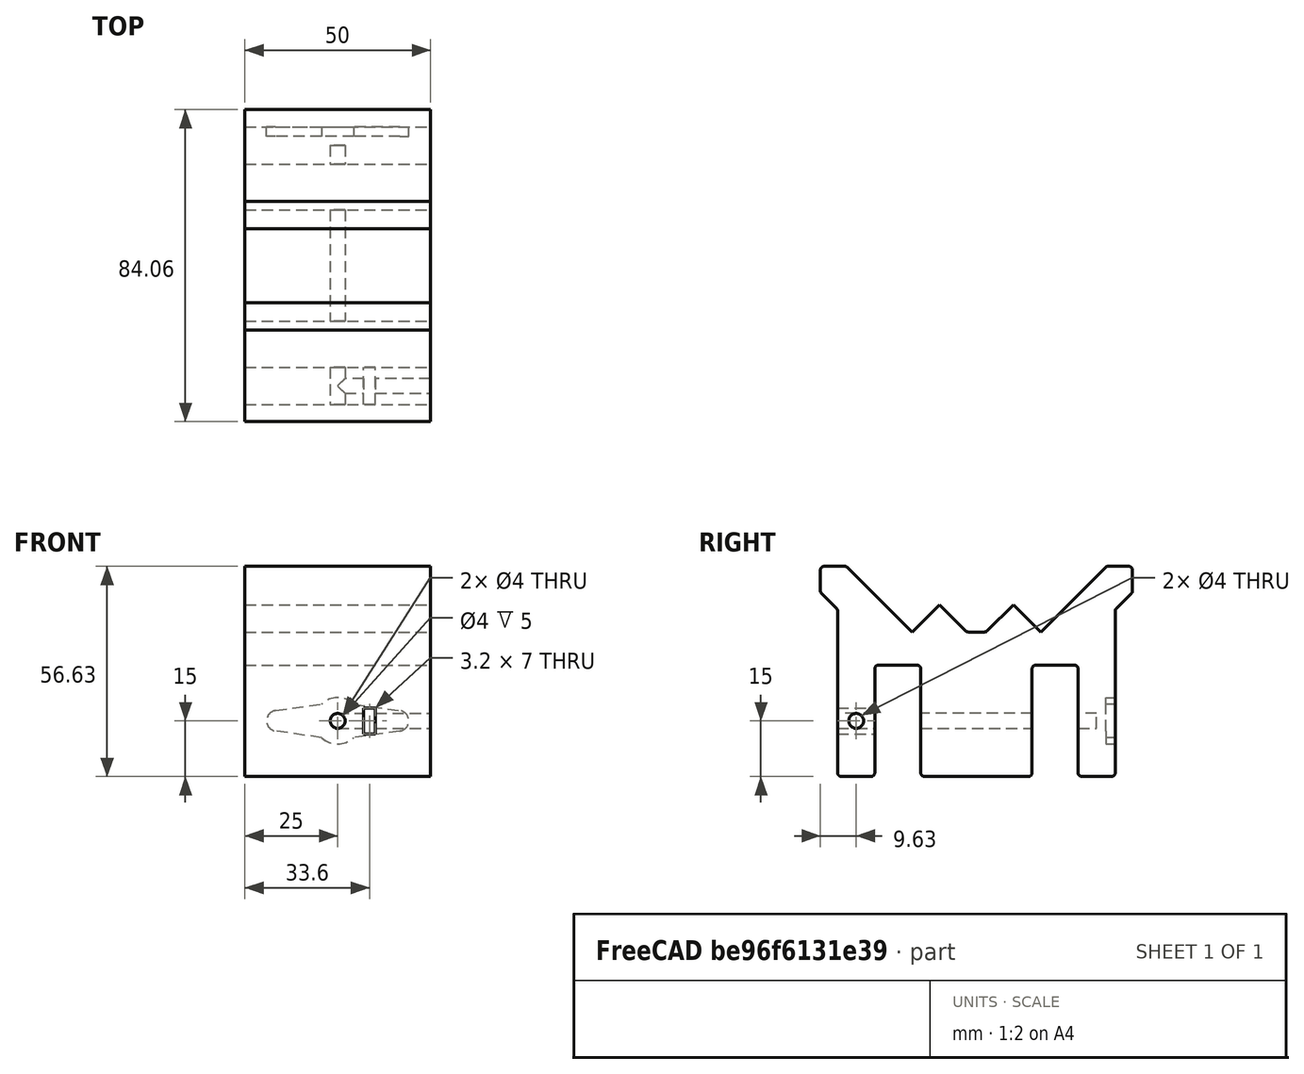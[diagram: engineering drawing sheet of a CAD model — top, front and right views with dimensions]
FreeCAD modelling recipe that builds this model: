
FCSTD DOCUMENT  (FreeCAD 0.19R24267 +99 (Git))
Label: Lager
License: All rights reserved
LicenseURL: http://en.wikipedia.org/wiki/All_rights_reserved
objects: TechDraw::DrawViewDimension×24, Sketcher::SketchObject×5, PartDesign::Pocket×4, PartDesign::Fillet×3, TechDraw::DrawProjGroupItem×3, PartDesign::Pad×1, PartDesign::Body×1, TechDraw::DrawSVGTemplate×1, TechDraw::DrawProjGroup×1, TechDraw::DrawPage×1
note: 22 computed .brp shape members not serialized (recipe doc carries the construction recipe); baked Part::Feature solids carry a one-line shape summary decoded from their .brp

FEATURE [Sketcher::SketchObject] Sketch
  FullyConstrained = true
  MapMode = 5
  Placement = pos=(0,0,0) rot=(0.57735,0.57735,0.57735;2.0944rad)
  Support = -> [YZ_Plane]
  sketch-geometry (29):
    g0: LineSegment StartX=-37.4 StartY=0 StartZ=0 EndX=-37.4 EndY=45 EndZ=0
    g1: LineSegment StartX=-37.4 StartY=45 StartZ=0 EndX=-42.0316 EndY=49.6316 EndZ=0
    g2: LineSegment StartX=-42.0316 StartY=49.6316 StartZ=0 EndX=-42.0316 EndY=56.6316 EndZ=0
    g3: LineSegment StartX=-42.0316 StartY=56.6316 StartZ=0 EndX=-35.0316 EndY=56.6316 EndZ=0
    g4: LineSegment StartX=-35.0316 StartY=56.6316 StartZ=0 EndX=-17.3539 EndY=38.9539 EndZ=0
    g5: LineSegment StartX=-17.3539 StartY=38.9539 StartZ=0 EndX=-10 EndY=46.3078 EndZ=0
    g6: LineSegment StartX=-10 StartY=46.3078 StartZ=0 EndX=-2.64609 EndY=38.9539 EndZ=0
    g7: LineSegment StartX=-2.64609 StartY=38.9539 StartZ=0 EndX=2.64609 EndY=38.9539 EndZ=0
    g8: LineSegment StartX=2.64609 StartY=38.9539 StartZ=0 EndX=10 EndY=46.3078 EndZ=0
    g9: LineSegment StartX=10 StartY=46.3078 StartZ=0 EndX=17.3539 EndY=38.9539 EndZ=0
    g10: LineSegment StartX=17.3539 StartY=38.9539 StartZ=0 EndX=35.0316 EndY=56.6316 EndZ=0
    g11: LineSegment StartX=35.0316 StartY=56.6316 StartZ=0 EndX=42.0316 EndY=56.6316 EndZ=0
    g12: LineSegment StartX=42.0316 StartY=56.6316 StartZ=0 EndX=42.0316 EndY=49.6316 EndZ=0
    g13: LineSegment StartX=42.0316 StartY=49.6316 StartZ=0 EndX=37.4 EndY=45 EndZ=0
    g14: LineSegment StartX=37.4 StartY=45 StartZ=0 EndX=37.4 EndY=0 EndZ=0
    g15: LineSegment StartX=37.4 StartY=0 StartZ=0 EndX=27.4 EndY=0 EndZ=0
    g16: LineSegment StartX=27.4 StartY=0 StartZ=0 EndX=27.4 EndY=30 EndZ=0
    g17: LineSegment StartX=27.4 StartY=30 StartZ=0 EndX=15 EndY=30 EndZ=0
    g18: LineSegment StartX=15 StartY=30 StartZ=0 EndX=15 EndY=0 EndZ=0
    g19: LineSegment StartX=15 StartY=0 StartZ=0 EndX=-15 EndY=0 EndZ=0
    g20: LineSegment StartX=-15 StartY=0 StartZ=0 EndX=-15 EndY=30 EndZ=0
    g21: LineSegment StartX=-15 StartY=30 StartZ=0 EndX=-27.4 EndY=30 EndZ=0
    g22: LineSegment StartX=-27.4 StartY=30 StartZ=0 EndX=-27.4 EndY=0 EndZ=0
    g23: LineSegment StartX=-27.4 StartY=0 StartZ=0 EndX=-37.4 EndY=0 EndZ=0
    g24: Circle CenterX=0 CenterY=61.0566 CenterZ=0 NormalX=0 NormalY=0 NormalZ=1 AngleXU=0 Radius=17.5
    g25: LineSegment StartX=10 StartY=46.3078 StartZ=0 EndX=27.6777 EndY=63.9855 EndZ=0
    g26: LineSegment StartX=-10 StartY=46.3078 StartZ=0 EndX=-27.6777 EndY=63.9855 EndZ=0
    g27: LineSegment StartX=35.0316 StartY=56.6316 StartZ=0 EndX=27.6777 EndY=63.9855 EndZ=0
    g28: LineSegment StartX=-35.0316 StartY=56.6316 StartZ=0 EndX=-27.6777 EndY=63.9855 EndZ=0
  constraints (76):
    c: Vertical(g0)
    c: Coincident(g0,g1)
    c: Coincident(g1,g2)
    c: Coincident(g2,g3)
    c: Horizontal(g3)
    c: Coincident(g3,g4)
    c: Coincident(g4,g5)
    c: Coincident(g5,g6)
    c: Coincident(g6,g7)
    c: Coincident(g7,g8)
    c: Coincident(g8,g9)
    c: Coincident(g9,g10)
    c: Coincident(g10,g11)
    c: Coincident(g11,g12)
    c: Vertical(g12)
    c: Coincident(g12,g13)
    c: Coincident(g13,g14)
    c: Coincident(g14,g15)
    c: Coincident(g15,g16)
    c: Vertical(g16)
    c: Coincident(g16,g17)
    c: Horizontal(g17)
    c: Coincident(g17,g18)
    c: Vertical(g18)
    c: Coincident(g18,g19)
    c: Horizontal(g19)
    c: Coincident(g19,g20)
    c: Coincident(g20,g21)
    c: Coincident(g21,g22)
    c: Vertical(g22)
    c: Coincident(g22,g23)
    c: Coincident(g23,g0)
    c: Vertical(g20)
    c: Horizontal(g21)
    c: DistanceX(g17,g17) = 12.4
    c: Horizontal(g15)
    c: Horizontal(g23)
    c: Angle(g1,g0) = 2.35619
    c: Symmetric(g21,g16,g-2)
    c: Symmetric(g0,g14,g-2)
    c: DistanceX(g5,g8) = 20
    c: DistanceX(g19,g19) = 30
    c: DistanceX(g23,g23) = 10
    c: DistanceX(g10,g11) = 7
    c: DistanceY(g14,g14) = 45
    c: Symmetric(g13,g0,g-2)
    c: DistanceY(g12,g12) = 7
    c: Symmetric(g7,g6,g-2)
    c: Symmetric(g9,g4,g-2)
    c: DistanceY(g20,g20) = 30
    c: PointOnObject(g18,g-1)
    c: Parallel(g6,g1)
    c: Symmetric(g1,g12,g-2)
    c: Symmetric(g11,g2,g-2)
    c: Equal(g17,g21)
    c: Horizontal(g22,g19)
    c: Parallel(g1,g4)
    c: Angle(g5,g4) = 1.5708
    c: Distance(g4,g3) = 25
    c: Symmetric(g10,g3,g-2)
    c: Symmetric(g5,g8,g-2)
    c: Distance(g9) = 10.4
    c: Horizontal(g4,g6)
    c: PointOnObject(g24,g-2)
    c: Diameter(g24) = 35
    c: Coincident(g25,g8)
    c: Coincident(g26,g5)
    c: Coincident(g27,g10)
    c: Coincident(g27,g25)
    c: Coincident(g28,g3)
    c: Coincident(g28,g26)
    c: Equal(g10,g25)
    c: Equal(g9,g27)
    c: Equal(g4,g26)
    c: Equal(g28,g5)
    c: Tangent(g24,g25)
FEATURE [PartDesign::Pad] Pad
  Direction = (1,1,1)
  Length = 50
  Length2 = 100
  Placement = pos=(0,0,0) rot=(0.57735,0.57735,0.57735;2.0944rad)
  Profile = -> Sketch
  Type = 0
FEATURE [Sketcher::SketchObject] Sketch001
  ExternalGeometry = -> [Pad]
  FullyConstrained = true
  MapMode = 5
  Placement = pos=(-1.65e-14,-37.4,8.2e-15) rot=(-0.57735,-0.57735,0.57735;4.18879rad)
  Support = -> [Pad]
  sketch-geometry (2):
    g0: LineSegment StartX=-15 StartY=25 StartZ=0 EndX=-8.9e-15 EndY=25 EndZ=0
    g1: Circle CenterX=-15 CenterY=25 CenterZ=0 NormalX=0 NormalY=0 NormalZ=1 AngleXU=0 Radius=2
  constraints (5):
    c: Horizontal(g0)
    c: DistanceX(g0,g0) = 15
    c: Coincident(g1,g0)
    c: Symmetric(g-3,g-1,g0)
    c: Diameter(g1) = 4
FEATURE [PartDesign::Pocket] Pocket  label="Achsenloch"
  BaseFeature = -> Pad
  Length = 69.8
  Length2 = 100
  Offset = 2
  Placement = pos=(0,0,0) rot=(0.57735,0.57735,0.57735;2.0944rad)
  Profile = -> Sketch001
  Type = 0
  expr: Offset = 2
  expr: Length = 74.8 - 5
FEATURE [Sketcher::SketchObject] Sketch002
  ExternalGeometry = -> [Pocket]
  FullyConstrained = true
  MapMode = 5
  Placement = pos=(1.65e-14,37.4,-8.2e-15) rot=(0.57735,0.57735,0.57735;4.18879rad)
  Support = -> [Pocket]
  sketch-geometry (9):
    g0: LineSegment StartX=12.25 StartY=41.7602 StartZ=0 EndX=10.5 EndY=29.3373 EndZ=0
    g1: LineSegment StartX=10.5 StartY=20.6627 StartZ=0 EndX=12.25 EndY=8.23976 EndZ=0
    g2: ArcOfCircle CenterX=15 CenterY=8.62715 CenterZ=0 NormalX=0 NormalY=0 NormalZ=1 AngleXU=0 Radius=2.77715 StartAngle=3.28154 EndAngle=6.14324
    g3: LineSegment StartX=17.75 StartY=8.23976 StartZ=0 EndX=19.5 EndY=20.6627 EndZ=0
    g4: LineSegment StartX=19.5 StartY=29.3373 StartZ=0 EndX=17.75 EndY=41.7602 EndZ=0
    g5: ArcOfCircle CenterX=15 CenterY=41.3728 CenterZ=0 NormalX=0 NormalY=0 NormalZ=1 AngleXU=0 Radius=2.77715 StartAngle=0.139948 EndAngle=3.00164
    g6: ArcOfCircle CenterX=15 CenterY=25 CenterZ=0 NormalX=0 NormalY=0 NormalZ=1 AngleXU=0 Radius=6.25 StartAngle=5.51619 EndAngle=7.05018
    g7: ArcOfCircle CenterX=15 CenterY=25 CenterZ=0 NormalX=0 NormalY=0 NormalZ=1 AngleXU=0 Radius=6.25 StartAngle=2.3746 EndAngle=3.90859
    g8: LineSegment StartX=15 StartY=44.15 StartZ=0 EndX=15 EndY=5.85 EndZ=0
  constraints (25):
    c: DistanceX(g0,g4) = 9
    c: Coincident(g6,g4)
    c: Coincident(g6,g3)
    c: Coincident(g7,g6)
    c: Coincident(g7,g0)
    c: Coincident(g7,g1)
    c: Diameter(g6) = 12.5
    c: Equal(g7,g6)
    c: PointOnObject(g8,g5)
    c: PointOnObject(g8,g2)
    c: Vertical(g8)
    c: PointOnObject(g2,g8)
    c: DistanceY(g3,g4) = 8.67468
    c: Tangent(g5,g4) = -1.5708
    c: Tangent(g5,g0) = -1.5708
    c: Tangent(g1,g2) = -1.5708
    c: Tangent(g2,g3) = -1.5708
    c: Horizontal(g1,g3)
    c: Vertical(g4,g3)
    c: Horizontal(g0,g4)
    c: Symmetric(g8,g8,g6)
    c: DistanceY(g8,g8) = 38.3
    c: Symmetric(g2,g5,g6)
    c: DistanceX(g0,g4) = 5.5
    c: Coincident(g6,g-5)
FEATURE [PartDesign::Pocket] Pocket001  label="Servo-Halter"
  BaseFeature = -> Pocket
  Length = 2.5
  Length2 = 100
  Placement = pos=(0,0,0) rot=(0.57735,0.57735,0.57735;2.0944rad)
  Profile = -> Sketch002
  Type = 0
FEATURE [PartDesign::Fillet] Fillet  label="Abrundungen unten"
  Base = -> Pocket001 [Edge69,Edge78,Edge82,Edge84,Edge6,Edge1]
  BaseFeature = -> Pocket001
  Placement = pos=(0,0,0) rot=(0.57735,0.57735,0.57735;2.0944rad)
  Radius = 1
  SupportTransform = false
FEATURE [PartDesign::Fillet] Fillet001  label="Abrundungen innen"
  Base = -> Fillet [Edge72,Edge74,Edge85,Edge88]
  BaseFeature = -> Fillet
  Placement = pos=(0,0,0) rot=(0.57735,0.57735,0.57735;2.0944rad)
  Radius = 1
  SupportTransform = false
FEATURE [PartDesign::Fillet] Fillet002  label="Abrundungen oben"
  Base = -> Fillet001 [Edge59,Edge63,Edge54,Edge80,Edge84,Edge101,Edge113,Edge103]
  BaseFeature = -> Fillet001
  Placement = pos=(0,0,0) rot=(0.57735,0.57735,0.57735;2.0944rad)
  Radius = 1
  SupportTransform = false
FEATURE [Sketcher::SketchObject] Sketch003
  ExternalGeometry = -> [Fillet002]
  FullyConstrained = true
  MapMode = 5
  Placement = pos=(50,-1.1e-14,1.7e-14) rot=(0.57735,0.57735,0.57735;2.0944rad)
  Support = -> [Fillet002]
  sketch-geometry (2):
    g0: Circle CenterX=-32.4 CenterY=15 CenterZ=0 NormalX=0 NormalY=0 NormalZ=1 AngleXU=0 Radius=2
    g1: LineSegment StartX=-37.4 StartY=15 StartZ=0 EndX=-27.4 EndY=15 EndZ=0
  constraints (5):
    c: Horizontal(g1)
    c: Symmetric(g1,g1,g0)
    c: Diameter(g0) = 4
    c: Symmetric(g-3,g-3,g1)
    c: PointOnObject(g1,g-4)
FEATURE [PartDesign::Pocket] Pocket002  label="Halteschraube"
  BaseFeature = -> Fillet002
  Length = 25
  Length2 = 100
  Placement = pos=(0,0,0) rot=(0.57735,0.57735,0.57735;2.0944rad)
  Profile = -> Sketch003
  Type = 0
FEATURE [Sketcher::SketchObject] Sketch004
  ExternalGeometry = -> [Pocket002]
  FullyConstrained = true
  MapMode = 5
  Placement = pos=(-1.65e-14,-37.4,8.2e-15) rot=(-0.57735,-0.57735,0.57735;4.18879rad)
  Support = -> [Pocket002]
  sketch-geometry (7):
    g0: LineSegment StartX=-18.5 StartY=32 StartZ=0 EndX=-11.5 EndY=32 EndZ=0
    g1: LineSegment StartX=-11.5 StartY=32 StartZ=0 EndX=-11.5 EndY=35.2 EndZ=0
    g2: LineSegment StartX=-11.5 StartY=35.2 StartZ=0 EndX=-18.5 EndY=35.2 EndZ=0
    g3: LineSegment StartX=-18.5 StartY=35.2 StartZ=0 EndX=-18.5 EndY=32 EndZ=0
    g4: LineSegment StartX=-15 StartY=25 StartZ=0 EndX=-15 EndY=33.6 EndZ=0
    g5: GeomPoint X=-15 Y=27 Z=0
    g6: GeomPoint X=-15 Y=32 Z=0
  constraints (18):
    c: Coincident(g0,g1)
    c: Coincident(g1,g2)
    c: Coincident(g2,g3)
    c: Coincident(g3,g0)
    c: Horizontal(g0)
    c: Horizontal(g2)
    c: Vertical(g1)
    c: Vertical(g3)
    c: Coincident(g4,g-3)
    c: Vertical(g4)
    c: Symmetric(g0,g1,g4)
    c: DistanceX(g2,g2) = 7
    c: DistanceY(g3,g3) = 3.2
    c: PointOnObject(g5,g4)
    c: PointOnObject(g5,g-3)
    c: PointOnObject(g6,g4)
    c: PointOnObject(g6,g0)
    c: DistanceY(g5,g6) = 5
FEATURE [PartDesign::Pocket] Pocket003  label="Mutterschacht"
  BaseFeature = -> Pocket002
  Length = 0
  Length2 = 100
  Placement = pos=(0,0,0) rot=(0.57735,0.57735,0.57735;2.0944rad)
  Profile = -> Sketch004
  Type = 3
  UpToFace = -> Pocket002 [Face10]
FEATURE [PartDesign::Body] Body
  Group = -> [Sketch,Pad,Sketch001,Pocket,Sketch002,Pocket001,Fillet,Fillet001,Fillet002,Sketch003,Pocket002,Sketch004,Pocket003]
  Origin = -> Origin
  Tip = -> Pocket003
FEATURE [TechDraw::DrawSVGTemplate] Template
  EditableTexts = APPROVER_NAME=APPROVER NAME; AUTHOR_NAME=AUTHOR NAME; DATE=YYYY-MM-DD; DN=DN; DOCUMENT_TYPE=Mechanical assembly drawing; OWNER_NAME=OWNER NAME; PM=PM; PN=PN; REVISION=REV A; RIGHTS=(R) DO NOT DUPLICATE THIS DRAWING TO THIRD PARTIES WITHOUT OWNER'S PERMISSION!; SCALE=M x:x; SHEET=99 of 99; SIZE=A3; TITLELINE-1=FreeCAD; TOLERANCE=+/- ?
  Height = 297
  Orientation = 1
  Width = 420
FEATURE [TechDraw::DrawProjGroupItem] ProjItem  label="Front"
  CoarseView = false
  Direction = (1,0,0)
  Focus = 100
  HardHidden = true
  IsoCount = 0
  IsoHidden = false
  IsoVisible = false
  LockPosition = true
  Perspective = false
  Rotation = 0
  RotationVector = (0,1,0)
  ScaleType = 2
  SeamHidden = false
  SeamVisible = true
  SmoothHidden = false
  SmoothVisible = true
  Source = -> [Body]
  Type = 0
  X = 0
  XDirection = (0,1,0)
  Y = 0
FEATURE [TechDraw::DrawProjGroupItem] ProjItem001  label="Left"
  CoarseView = false
  Direction = (1e-16,-1,0)
  Focus = 100
  HardHidden = false
  IsoCount = 0
  IsoHidden = false
  IsoVisible = false
  LockPosition = false
  Perspective = false
  Rotation = 0
  RotationVector = (1,0,0)
  ScaleType = 2
  SeamHidden = false
  SeamVisible = true
  SmoothHidden = false
  SmoothVisible = true
  Source = -> [Body]
  Type = 1
  X = 82.0316
  XDirection = (1,1e-16,0)
  Y = 0
FEATURE [TechDraw::DrawProjGroupItem] ProjItem002  label="Bottom"
  CoarseView = false
  Direction = (0,0,-1)
  Focus = 100
  HardHidden = false
  IsoCount = 0
  IsoHidden = false
  IsoVisible = false
  LockPosition = false
  Perspective = false
  Rotation = 0
  RotationVector = (1,0,0)
  ScaleType = 2
  SeamHidden = false
  SeamVisible = true
  SmoothHidden = false
  SmoothVisible = true
  Source = -> [Body]
  Type = 5
  X = 0
  XDirection = (0,1,0)
  Y = 68.3158
FEATURE [TechDraw::DrawProjGroup] ProjGroup
  Anchor = -> ProjItem
  AutoDistribute = true
  LockPosition = false
  ProjectionType = 0
  Rotation = 0
  ScaleType = 0
  Source = -> [Body]
  Views = -> [ProjItem,ProjItem001,ProjItem002]
  X = 180.965
  Y = 137.456
  spacingX = 15
  spacingY = 15
FEATURE [TechDraw::DrawViewDimension] Dimension
  Arbitrary = false
  ArbitraryTolerances = false
  EqualTolerance = true
  FormatSpec = %.2f
  FormatSpecOverTolerance = %+.2f
  FormatSpecUnderTolerance = %+.2f
  Inverted = false
  LockPosition = false
  MeasureType = 1
  OverTolerance = 0
  References2D = -> [ProjItem]
  Rotation = 0
  ScaleType = 0
  TheoreticalExact = false
  Type = 1
  UnderTolerance = 0
  X = -1.02541
  Y = -49.8748
FEATURE [TechDraw::DrawViewDimension] Dimension001
  Arbitrary = false
  ArbitraryTolerances = false
  EqualTolerance = true
  FormatSpec = %.2f
  FormatSpecOverTolerance = %+.2f
  FormatSpecUnderTolerance = %+.2f
  Inverted = false
  LockPosition = false
  MeasureType = 1
  OverTolerance = 0
  References2D = -> [ProjItem]
  Rotation = 0
  ScaleType = 0
  TheoreticalExact = false
  Type = 1
  UnderTolerance = 0
  X = -21.6102
  Y = -58.6933
FEATURE [TechDraw::DrawViewDimension] Dimension002
  Arbitrary = false
  ArbitraryTolerances = false
  EqualTolerance = true
  FormatSpec = %.2f
  FormatSpecOverTolerance = %+.2f
  FormatSpecUnderTolerance = %+.2f
  Inverted = false
  LockPosition = false
  MeasureType = 1
  OverTolerance = 0
  References2D = -> [ProjItem]
  Rotation = 0
  ScaleType = 0
  TheoreticalExact = false
  Type = 1
  UnderTolerance = 0
  X = -33.0152
  Y = -50.0799
FEATURE [TechDraw::DrawViewDimension] Dimension004
  Arbitrary = false
  ArbitraryTolerances = false
  EqualTolerance = true
  FormatSpec = %.2f
  FormatSpecOverTolerance = %+.2f
  FormatSpecUnderTolerance = %+.2f
  Inverted = false
  LockPosition = false
  MeasureType = 1
  OverTolerance = 0
  References2D = -> [ProjItem]
  Rotation = 0
  ScaleType = 0
  TheoreticalExact = false
  Type = 1
  UnderTolerance = 0
  X = -54.1777
  Y = -38.5681
FEATURE [TechDraw::DrawViewDimension] Dimension005
  Arbitrary = false
  ArbitraryTolerances = false
  EqualTolerance = true
  FormatSpec = %.2f
  FormatSpecOverTolerance = %+.2f
  FormatSpecUnderTolerance = %+.2f
  Inverted = false
  LockPosition = false
  MeasureType = 1
  OverTolerance = 0
  References2D = -> [ProjItem]
  Rotation = 0
  ScaleType = 0
  TheoreticalExact = false
  Type = 2
  UnderTolerance = 0
  X = 84.479
  Y = -2.94667
FEATURE [TechDraw::DrawViewDimension] Dimension006
  Arbitrary = false
  ArbitraryTolerances = false
  EqualTolerance = true
  FormatSpec = %.2f
  FormatSpecOverTolerance = %+.2f
  FormatSpecUnderTolerance = %+.2f
  Inverted = false
  LockPosition = false
  MeasureType = 1
  OverTolerance = 0
  References2D = -> [ProjItem]
  Rotation = 0
  ScaleType = 0
  TheoreticalExact = false
  Type = 2
  UnderTolerance = 0
  X = 93.6523
  Y = 9.56623
FEATURE [TechDraw::DrawViewDimension] Dimension007
  Arbitrary = false
  ArbitraryTolerances = false
  EqualTolerance = true
  FormatSpec = %.2f
  FormatSpecOverTolerance = %+.2f
  FormatSpecUnderTolerance = %+.2f
  Inverted = false
  LockPosition = false
  MeasureType = 1
  OverTolerance = 0
  References2D = -> [ProjItem]
  Rotation = 0
  ScaleType = 0
  TheoreticalExact = false
  Type = 2
  UnderTolerance = 0
  X = 84.5988
  Y = 36.0973
FEATURE [TechDraw::DrawViewDimension] Dimension008
  Arbitrary = false
  ArbitraryTolerances = false
  EqualTolerance = true
  FormatSpec = %.2f
  FormatSpecOverTolerance = %+.2f
  FormatSpecUnderTolerance = %+.2f
  Inverted = false
  LockPosition = false
  MeasureType = 1
  OverTolerance = 0
  References2D = -> [ProjItem]
  Rotation = 0
  ScaleType = 0
  TheoreticalExact = false
  Type = 2
  UnderTolerance = 0
  X = 58.1623
  Y = -11.8802
FEATURE [TechDraw::DrawViewDimension] Dimension009
  Arbitrary = false
  ArbitraryTolerances = false
  EqualTolerance = true
  FormatSpec = %.2f
  FormatSpecOverTolerance = %+.2f
  FormatSpecUnderTolerance = %+.2f
  Inverted = false
  LockPosition = false
  MeasureType = 1
  OverTolerance = 0
  References2D = -> [ProjItem]
  Rotation = 0
  ScaleType = 0
  TheoreticalExact = false
  Type = 6
  UnderTolerance = 0
  X = 17.5657
  Y = 21.5336
FEATURE [TechDraw::DrawViewDimension] Dimension010
  Arbitrary = false
  ArbitraryTolerances = false
  EqualTolerance = true
  FormatSpec = %.2f
  FormatSpecOverTolerance = %+.2f
  FormatSpecUnderTolerance = %+.2f
  Inverted = false
  LockPosition = false
  MeasureType = 1
  OverTolerance = 0
  References2D = -> [ProjItem]
  Rotation = 0
  ScaleType = 0
  TheoreticalExact = false
  Type = 6
  UnderTolerance = 0
  X = -50.3072
  Y = 21.7045
FEATURE [TechDraw::DrawViewDimension] Dimension011
  Arbitrary = false
  ArbitraryTolerances = false
  EqualTolerance = true
  FormatSpec = %.2f
  FormatSpecOverTolerance = %+.2f
  FormatSpecUnderTolerance = %+.2f
  Inverted = false
  LockPosition = false
  MeasureType = 1
  OverTolerance = 0
  References2D = -> [ProjItem]
  Rotation = 0
  ScaleType = 0
  TheoreticalExact = false
  Type = 1
  UnderTolerance = 0
  X = 42.1711
  Y = 47.975
FEATURE [TechDraw::DrawViewDimension] Dimension012
  Arbitrary = false
  ArbitraryTolerances = false
  EqualTolerance = true
  FormatSpec = %.2f
  FormatSpecOverTolerance = %+.2f
  FormatSpecUnderTolerance = %+.2f
  Inverted = false
  LockPosition = false
  MeasureType = 1
  OverTolerance = 0
  References2D = -> [ProjItem]
  Rotation = 0
  ScaleType = 0
  TheoreticalExact = false
  Type = 1
  UnderTolerance = 0
  X = 27.0642
  Y = 59.1644
FEATURE [TechDraw::DrawViewDimension] Dimension013
  Arbitrary = false
  ArbitraryTolerances = false
  EqualTolerance = true
  FormatSpec = %.2f
  FormatSpecOverTolerance = %+.2f
  FormatSpecUnderTolerance = %+.2f
  Inverted = false
  LockPosition = false
  MeasureType = 1
  OverTolerance = 0
  References2D = -> [ProjItem]
  Rotation = 0
  ScaleType = 0
  TheoreticalExact = false
  Type = 1
  UnderTolerance = 0
  X = 10.4684
  Y = 47.9755
FEATURE [TechDraw::DrawViewDimension] Dimension014
  Arbitrary = false
  ArbitraryTolerances = false
  EqualTolerance = true
  FormatSpec = %.2f
  FormatSpecOverTolerance = %+.2f
  FormatSpecUnderTolerance = %+.2f
  Inverted = false
  LockPosition = false
  MeasureType = 1
  OverTolerance = 0
  References2D = -> [ProjItem]
  Rotation = 0
  ScaleType = 0
  TheoreticalExact = false
  Type = 1
  UnderTolerance = 0
  X = -14.1103
  Y = 40.3571
FEATURE [TechDraw::DrawViewDimension] Dimension015
  Arbitrary = false
  ArbitraryTolerances = false
  EqualTolerance = true
  FormatSpec = %.2f
  FormatSpecOverTolerance = %+.2f
  FormatSpecUnderTolerance = %+.2f
  Inverted = false
  LockPosition = false
  MeasureType = 1
  OverTolerance = 0
  References2D = -> [ProjItem]
  Rotation = 0
  ScaleType = 0
  TheoreticalExact = false
  Type = 1
  UnderTolerance = 0
  X = 0.854508
  Y = 59.2078
FEATURE [TechDraw::DrawViewDimension] Dimension016
  Arbitrary = false
  ArbitraryTolerances = false
  EqualTolerance = true
  FormatSpec = %.2f
  FormatSpecOverTolerance = %+.2f
  FormatSpecUnderTolerance = %+.2f
  Inverted = false
  LockPosition = false
  MeasureType = 1
  OverTolerance = 0
  References2D = -> [ProjItem001]
  Rotation = 0
  ScaleType = 0
  TheoreticalExact = false
  Type = 1
  UnderTolerance = 0
  X = 0.210414
  Y = -70.8868
FEATURE [TechDraw::DrawViewDimension] Dimension017
  Arbitrary = false
  ArbitraryTolerances = false
  EqualTolerance = true
  FormatSpec = %.2f
  FormatSpecOverTolerance = %+.2f
  FormatSpecUnderTolerance = %+.2f
  Inverted = false
  LockPosition = false
  MeasureType = 1
  OverTolerance = 0
  References2D = -> [ProjItem001]
  Rotation = 0
  ScaleType = 0
  TheoreticalExact = false
  Type = 1
  UnderTolerance = 0
  X = -11.4401
  Y = -59.2868
FEATURE [TechDraw::DrawViewDimension] Dimension018
  Arbitrary = false
  ArbitraryTolerances = false
  EqualTolerance = true
  FormatSpec = %.2f
  FormatSpecOverTolerance = %+.2f
  FormatSpecUnderTolerance = %+.2f
  Inverted = false
  LockPosition = false
  MeasureType = 1
  OverTolerance = 0
  References2D = -> [ProjItem001]
  Rotation = 0
  ScaleType = 0
  TheoreticalExact = false
  Type = 2
  UnderTolerance = 0
  X = 56.6765
  Y = -1.57259
FEATURE [TechDraw::DrawViewDimension] Dimension019
  Arbitrary = false
  ArbitraryTolerances = false
  EqualTolerance = true
  FormatSpec = %.2f
  FormatSpecOverTolerance = %+.2f
  FormatSpecUnderTolerance = %+.2f
  Inverted = false
  LockPosition = false
  MeasureType = 1
  OverTolerance = 0
  References2D = -> [ProjItem001]
  Rotation = 0
  ScaleType = 0
  TheoreticalExact = false
  Type = 2
  UnderTolerance = 0
  X = 45.4573
  Y = -21.2179
FEATURE [TechDraw::DrawViewDimension] Dimension020
  Arbitrary = false
  ArbitraryTolerances = false
  EqualTolerance = true
  FormatSpec = %.2f
  FormatSpecOverTolerance = %+.2f
  FormatSpecUnderTolerance = %+.2f
  Inverted = false
  LockPosition = false
  MeasureType = 1
  OverTolerance = 0
  References2D = -> [ProjItem001]
  Rotation = 0
  ScaleType = 0
  TheoreticalExact = false
  Type = 2
  UnderTolerance = 0
  X = 35.5861
  Y = 0.837533
FEATURE [TechDraw::DrawViewDimension] Dimension021
  Arbitrary = false
  ArbitraryTolerances = false
  EqualTolerance = true
  FormatSpec = %.2f
  FormatSpecOverTolerance = %+.2f
  FormatSpecUnderTolerance = %+.2f
  Inverted = false
  LockPosition = false
  MeasureType = 1
  OverTolerance = 0
  References2D = -> [ProjItem001]
  Rotation = 0
  ScaleType = 0
  TheoreticalExact = false
  Type = 1
  UnderTolerance = 0
  X = -9.30539
  Y = -48.3149
FEATURE [TechDraw::DrawViewDimension] Dimension022
  Arbitrary = false
  ArbitraryTolerances = false
  EqualTolerance = true
  FormatSpec = %.2f
  FormatSpecOverTolerance = %+.2f
  FormatSpecUnderTolerance = %+.2f
  Inverted = false
  LockPosition = false
  MeasureType = 1
  OverTolerance = 0
  References2D = -> [ProjItem001]
  Rotation = 0
  ScaleType = 0
  TheoreticalExact = false
  Type = 1
  UnderTolerance = 0
  X = 15.789
  Y = -59.2758
FEATURE [TechDraw::DrawViewDimension] Dimension023
  Arbitrary = false
  ArbitraryTolerances = false
  EqualTolerance = true
  FormatSpec = ⌀%.2f
  FormatSpecOverTolerance = %+.2f
  FormatSpecUnderTolerance = %+.2f
  Inverted = false
  LockPosition = false
  MeasureType = 1
  OverTolerance = 0
  References2D = -> [ProjItem]
  Rotation = 0
  ScaleType = 0
  TheoreticalExact = false
  Type = 5
  UnderTolerance = 0
  X = -46.1188
  Y = 0.344537
FEATURE [TechDraw::DrawViewDimension] Dimension024
  Arbitrary = false
  ArbitraryTolerances = false
  EqualTolerance = true
  FormatSpec = ⌀%.2f
  FormatSpecOverTolerance = %+.2f
  FormatSpecUnderTolerance = %+.2f
  Inverted = false
  LockPosition = false
  MeasureType = 1
  OverTolerance = 0
  References2D = -> [ProjItem001]
  Rotation = 0
  ScaleType = 0
  TheoreticalExact = false
  Type = 5
  UnderTolerance = 0
  X = -9.74549
  Y = 0
FEATURE [TechDraw::DrawPage] Page
  KeepUpdated = true
  NextBalloonIndex = 1
  ProjectionType = 0
  Template = -> Template
  Views = -> [ProjGroup,Dimension,Dimension001,Dimension002,Dimension004,Dimension005,Dimension006,Dimension007,Dimension008,Dimension009,Dimension010,Dimension011,Dimension012,Dimension013,Dimension014,Dimension015,Dimension016,Dimension017,Dimension018,Dimension019,Dimension020,Dimension021,Dimension022,Dimension023,Dimension024]
